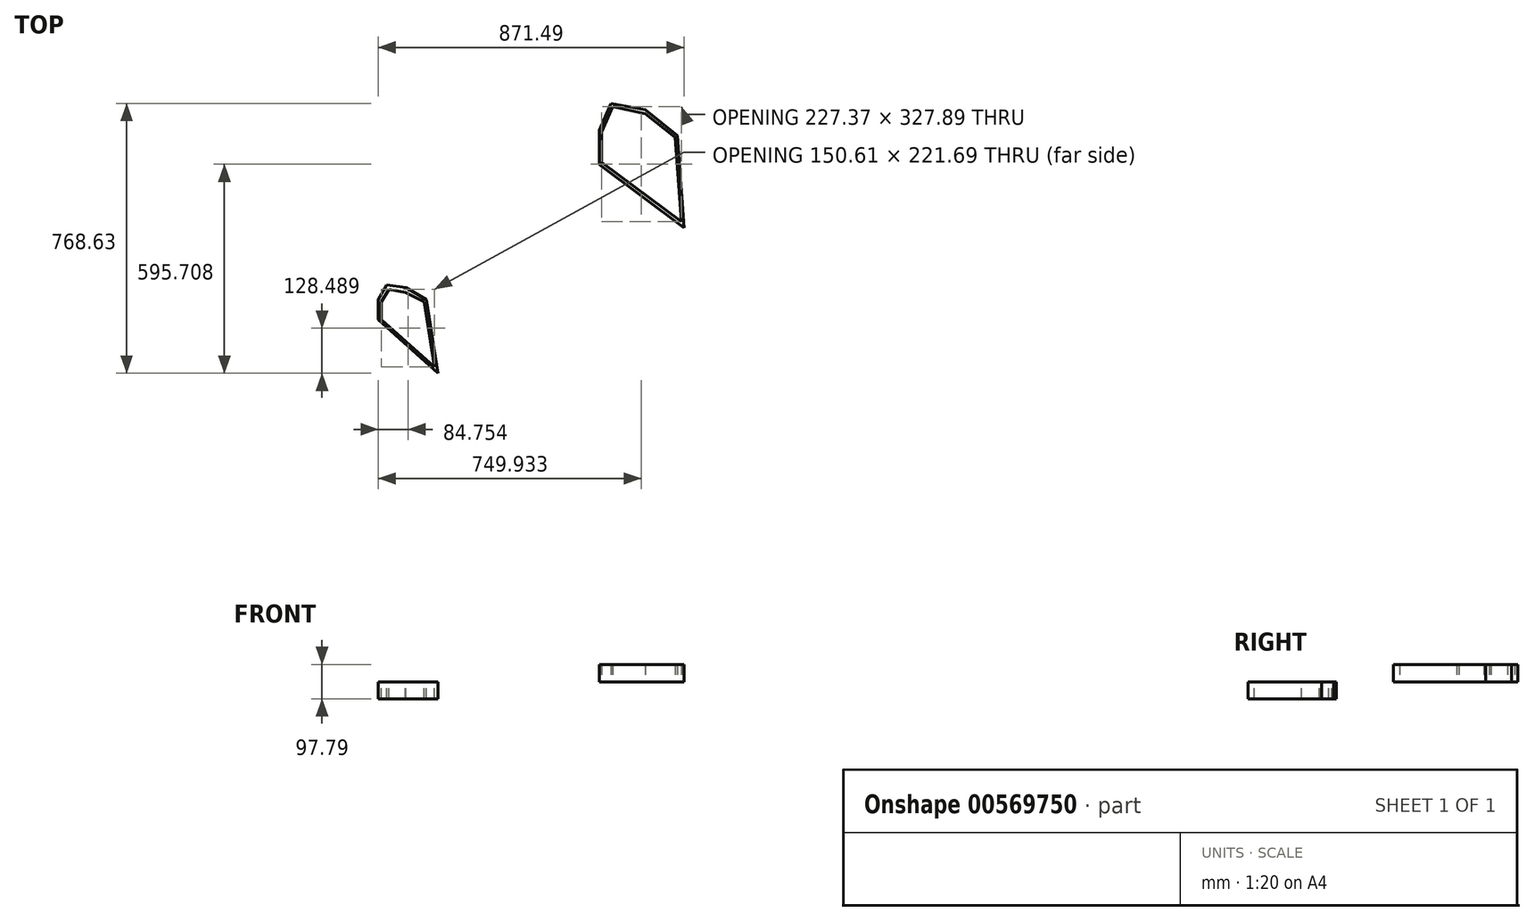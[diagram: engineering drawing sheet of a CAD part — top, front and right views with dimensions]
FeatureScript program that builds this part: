
annotation { "Feature Type Name" : "Feature", "Feature Type Description" : "" }
export const myFeature = defineFeature(function(context is Context, id is Id, definition is map)
    precondition{}
    {
        {
            var Q0;
            Q0=qCreatedBy(makeId("Top.planeOp"),FACE);
            var sketch = newSketch(context, id + "F0", { "sketchPlane" : qUnion([Q0])});
            skLineSegment(sketch, "E0", {"start": v(152.46, 548.29) * mm, "end": v(120.97, 501.32) * mm});
            skLineSegment(sketch, "E1", {"start": v(120.97, 501.32) * mm, "end": v(120.97, 441.04) * mm});
            skLineSegment(sketch, "E2", {"start": v(152.46, 548.29) * mm, "end": v(208.82, 548.29) * mm});
            skLineSegment(sketch, "E3", {"start": v(208.82, 548.29) * mm, "end": v(265.13, 518.75) * mm});
            skLineSegment(sketch, "E4", {"start": v(265.13, 518.75) * mm, "end": v(300.98, 307.08) * mm});
            skLineSegment(sketch, "E5", {"start": v(120.97, 441.04) * mm, "end": v(300.98, 307.08) * mm});
            skLineSegment(sketch, "E6", {"start": v(120.97, 441.04) * mm, "end": v(169.28, 441.04) * mm});
            skLineSegment(sketch, "E7", {"start": v(265.13, 518.75) * mm, "end": v(240.18, 471.18) * mm});
            skPoint(sketch, "E7.endSnap0", {"position": v(120.97, 471.18) * mm});
            skLineSegment(sketch, "E8", {"start": v(169.28, 441.04) * mm, "end": v(240.18, 471.18) * mm});
            skLineSegment(sketch, "E9", {"start": v(120.97, 501.32) * mm, "end": v(158.4, 501.32) * mm});
            skLineSegment(sketch, "E10", {"start": v(208.82, 548.29) * mm, "end": v(192.92, 517.98) * mm});
            skLineSegment(sketch, "E11", {"start": v(158.4, 501.32) * mm, "end": v(192.92, 517.98) * mm});
            skLineSegment(sketch, "E12", {"start": v(158.4, 501.32) * mm, "end": v(169.28, 441.04) * mm});
            skLineSegment(sketch, "E13", {"start": v(192.92, 517.98) * mm, "end": v(240.18, 471.18) * mm});
            skLineSegment(sketch, "E14", {"start": v(169.28, 441.04) * mm, "end": v(300.98, 307.08) * mm});
            skLineSegment(sketch, "E15", {"start": v(240.18, 471.18) * mm, "end": v(300.98, 307.08) * mm});
            skSolve(sketch);
        }
        {
            var Q0;
            Q0=qCreatedBy(makeId("Top.planeOp"),FACE);
            var sketch = newSketch(context, id + "F1", { "sketchPlane" : qUnion([Q0])});
            skLineSegment(sketch, "E16", {"start": v(-145.48, 442.86) * mm, "end": v(-91.13, 435.76) * mm});
            skLineSegment(sketch, "E17", {"start": v(-145.48, 442.86) * mm, "end": v(-170.33, 400.72) * mm});
            skLineSegment(sketch, "E18", {"start": v(-170.33, 400.72) * mm, "end": v(-170.33, 343.79) * mm});
            skLineSegment(sketch, "E19", {"start": v(-91.13, 435.76) * mm, "end": v(-32.64, 400.72) * mm});
            skLineSegment(sketch, "E20", {"start": v(-32.64, 400.72) * mm, "end": v(0, 191.32) * mm});
            skLineSegment(sketch, "E21", {"start": v(-170.33, 343.79) * mm, "end": v(0, 191.32) * mm});
            skLineSegment(sketch, "E22", {"start": v(-160.88, 343.79) * mm, "end": v(-10.27, 208.97) * mm});
            skLineSegment(sketch, "E23", {"start": v(-10.27, 208.97) * mm, "end": v(-39.27, 394.98) * mm});
            skLineSegment(sketch, "E24", {"start": v(-160.88, 343.79) * mm, "end": v(-160.88, 394.98) * mm});
            skLineSegment(sketch, "E25", {"start": v(-160.88, 394.98) * mm, "end": v(-139.85, 430.65) * mm});
            skLineSegment(sketch, "E26", {"start": v(-139.85, 430.65) * mm, "end": v(-92.48, 421.93) * mm});
            skLineSegment(sketch, "E27", {"start": v(-92.48, 421.93) * mm, "end": v(-39.27, 394.98) * mm});
            skSolve(sketch);
        }
        {
            var Q0;
            Q0=makeQuery(id+"F1.imprint","IMPRINT",FACE,{"disambiguationData":[TD([[makeQuery(id+"F1.imprint","IMPRINT",EDGE,{"derivedFrom":sQuery(id+"F1.wireOp",EDGE,"E16")}),-1.0]])]});
            extrude(context, id + "F2", {"entities" : qUnion([Q0]), "oppositeDirection" : true, "depth" : 48.26 * mm, "offsetDistance" : 25.4 * mm});
        }
        {
            var Q0;
            Q0=makeQuery(id+"F0.imprint","IMPRINT",FACE,{"disambiguationData":[TD([[makeQuery(id+"F0.imprint","IMPRINT",EDGE,{"derivedFrom":sQuery(id+"F0.wireOp",EDGE,"E8")}),1.0]])]});
            var sketch = newSketch(context, id + "F3", { "sketchPlane" : qUnion([Q0])});
            skLineSegment(sketch, "E28", {"start": v(459.5, 786.05) * mm, "end": v(459.5, 883.97) * mm});
            skLineSegment(sketch, "E29", {"start": v(459.5, 883.97) * mm, "end": v(492.72, 959.95) * mm});
            skLineSegment(sketch, "E30", {"start": v(492.72, 959.95) * mm, "end": v(590.68, 941.79) * mm});
            skLineSegment(sketch, "E31", {"start": v(590.68, 941.79) * mm, "end": v(681.59, 868.2) * mm});
            skLineSegment(sketch, "E32", {"start": v(681.59, 868.2) * mm, "end": v(701.16, 605.86) * mm});
            skLineSegment(sketch, "E33", {"start": v(459.5, 786.05) * mm, "end": v(701.16, 605.86) * mm});
            skLineSegment(sketch, "E34", {"start": v(465.92, 878.57) * mm, "end": v(498.33, 950.97) * mm});
            skLineSegment(sketch, "E35", {"start": v(465.92, 878.57) * mm, "end": v(465.92, 792.6) * mm});
            skLineSegment(sketch, "E36", {"start": v(465.92, 792.6) * mm, "end": v(693.29, 623.08) * mm});
            skLineSegment(sketch, "E37", {"start": v(693.29, 623.08) * mm, "end": v(675.35, 863.45) * mm});
            skLineSegment(sketch, "E38", {"start": v(590.68, 930.88) * mm, "end": v(675.35, 863.45) * mm});
            skLineSegment(sketch, "E39", {"start": v(498.33, 950.97) * mm, "end": v(590.68, 930.88) * mm});
            skSolve(sketch);
        }
        {
            var Q0;
            Q0=makeQuery(id+"F3.imprint","IMPRINT",FACE,{"disambiguationData":[TD([[makeQuery(id+"F3.imprint","IMPRINT",EDGE,{"derivedFrom":sQuery(id+"F3.wireOp",EDGE,"E28")}),-1.0]])]});
            extrude(context, id + "F4", {"entities" : qUnion([Q0]), "depth" : 49.53 * mm, "offsetDistance" : 25.4 * mm});
        }
    });
